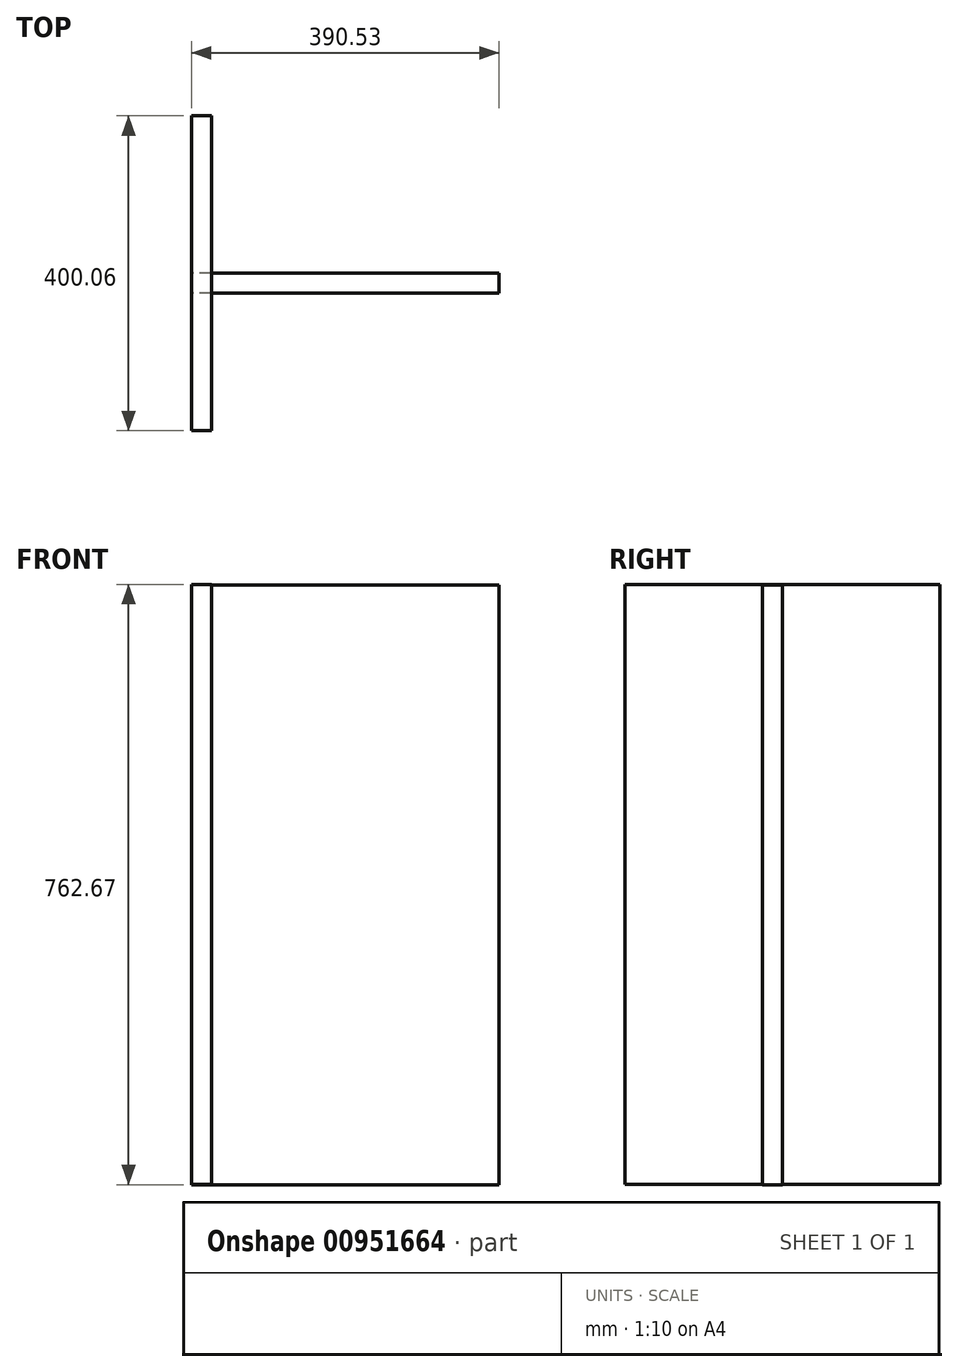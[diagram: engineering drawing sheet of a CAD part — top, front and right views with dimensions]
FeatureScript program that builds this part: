
annotation { "Feature Type Name" : "Feature", "Feature Type Description" : "" }
export const myFeature = defineFeature(function(context is Context, id is Id, definition is map)
    precondition{}
    {
        {
            var Q0;
            Q0=qCreatedBy(makeId("Right.planeOp"),FACE);
            var sketch = newSketch(context, id + "F0", { "sketchPlane" : qUnion([Q0])});
            skLineSegment(sketch, "E0.bottom", {"start": v(200.02, 381) * mm, "end": v(-200.03, 381) * mm});
            skLineSegment(sketch, "E0.top", {"start": v(200.03, -381) * mm, "end": v(-200.02, -381) * mm});
            skLineSegment(sketch, "E0.left", {"start": v(200.02, 381) * mm, "end": v(200.03, -381) * mm});
            skLineSegment(sketch, "E0.right", {"start": v(-200.03, 381) * mm, "end": v(-200.02, -381) * mm});
            skPoint(sketch, "E0.middle", {"position": v(0, 0) * mm});
            skSolve(sketch);
        }
        {
            var Q0;
            Q0=makeQuery(id+"F0.imprint","IMPRINT",FACE,{"disambiguationData":[TD([[makeQuery(id+"F0.imprint","IMPRINT",EDGE,{"derivedFrom":sQuery(id+"F0.wireOp",EDGE,"E0.bottom")}),1.0]])]});
            extrude(context, id + "F1", {"entities" : qUnion([Q0]), "depth" : 25.4 * mm, "offsetDistance" : 25.4 * mm});
        }
        {
            var Q0;
            Q0=qCreatedBy(makeId("Front.planeOp"),FACE);
            var sketch = newSketch(context, id + "F2", { "sketchPlane" : qUnion([Q0])});
            skLineSegment(sketch, "E1.bottom", {"start": v(0, 380.33) * mm, "end": v(390.53, 380.33) * mm});
            skLineSegment(sketch, "E1.top", {"start": v(0, -381.67) * mm, "end": v(390.53, -381.67) * mm});
            skLineSegment(sketch, "E1.left", {"start": v(0, 380.33) * mm, "end": v(0, -381.67) * mm});
            skLineSegment(sketch, "E1.right", {"start": v(390.53, 380.33) * mm, "end": v(390.53, -381.67) * mm});
            skSolve(sketch);
        }
        {
            var Q0;
            Q0=makeQuery(id+"F2.imprint","IMPRINT",FACE,{"disambiguationData":[TD([[makeQuery(id+"F2.imprint","IMPRINT",EDGE,{"derivedFrom":sQuery(id+"F2.wireOp",EDGE,"E1.bottom")}),-1.0]])]});
            extrude(context, id + "F3", {"entities" : qUnion([Q0]), "operationType" : NewBodyOperationType.ADD, "depth" : 25.4 * mm, "offsetDistance" : 25.4 * mm});
        }
    });
